# Revit family: 873-00-001-DN900-1000
name_source: partatom
category: Pipe Accessories
units: mm (PartAtom-declared; Revit-internal decimal feet)

## family parameters
Always vertical = Yes
Cut with Voids When Loaded = No
Part Type = Valve - Breaks Into
Round Connector Dimension = Use Diameter
Shared = No
Work Plane-Based = No

## types (4) — shared parameters
873-0900-00-041000 = DN900_PN10
873-0900-00-141000 = DN900_PN16
873-1000-00-041000 = DN1000_PN10
873-1000-00-141000 = DN1000_PN16
Angle = 22.50°
Body_Wallthicknss = 10 mm  [stored 0.0328084 ft]
Description_ = AVK DISMANTLING JOINT
Flange_thickness = 20 mm  [stored 0.0656168 ft]
Search_table = 873-00-001-DN900-1000
URL product pages = https://www.avkvalves.com

## per-type parameters (varying)
| type | A | DN | Id(Radius) | L | T | d1 | d2 |
| DN0900_PN10 | 325 mm  [stored 1.06627 ft] | 900 mm  [stored 2.95276 ft] | 450 mm  [stored 1.47638 ft] | 500 mm  [stored 1.64042 ft] | 30 mm  [stored 0.0984252 ft] | 1050 mm  [stored 3.44488 ft] | 558 mm |
| DN0900_PN16 | 325 mm  [stored 1.06627 ft] | 900 mm  [stored 2.95276 ft] | 450 mm  [stored 1.47638 ft] | 530 mm  [stored 1.73885 ft] | 36 mm  [stored 0.11811 ft] | 1050 mm  [stored 3.44488 ft] | 563 mm |
| DN1000_PN10 | 335 mm  [stored 1.09908 ft] | 1000 mm  [stored 3.28084 ft] | 500 mm  [stored 1.64042 ft] | 545 mm  [stored 1.78806 ft] | 33 mm  [stored 0.108268 ft] | 1160 mm  [stored 3.80577 ft] | 615 mm  [stored 2.01772 ft] |
| DN1000_PN16 | 335 mm  [stored 1.09908 ft] | 1000 mm  [stored 3.28084 ft] | 500 mm  [stored 1.64042 ft] | 570 mm  [stored 1.87008 ft] | 39 mm  [stored 0.127953 ft] | 1170 mm  [stored 3.83858 ft] | 628 mm |

note: [stored X ft] marks values corroborated as IEEE doubles in the binary element streams (Revit-internal decimal feet)

## geometry (parser evidence)
native form markers: Sweep x8
no freeform markers — native parametric forms only
